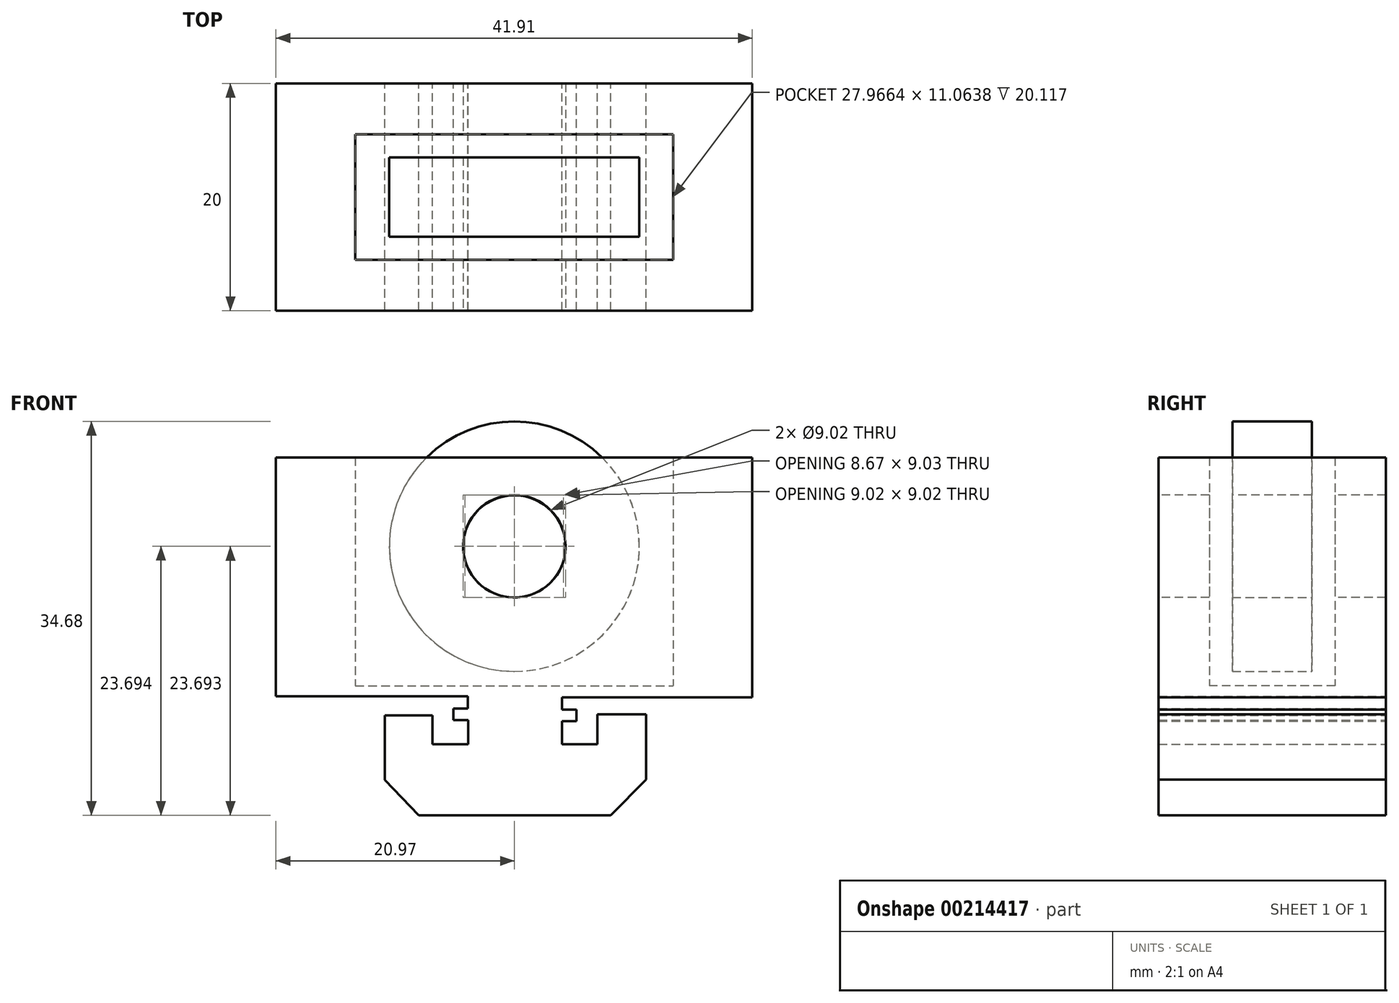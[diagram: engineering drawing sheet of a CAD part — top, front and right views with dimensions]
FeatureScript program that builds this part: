
annotation { "Feature Type Name" : "Feature", "Feature Type Description" : "" }
export const myFeature = defineFeature(function(context is Context, id is Id, definition is map)
    precondition{}
    {
        {
            var Q0;
            Q0=qCreatedBy(makeId("Front.planeOp"),FACE);
            var sketch = newSketch(context, id + "F0", { "sketchPlane" : qUnion([Q0])});
            skLineSegment(sketch, "E0", {"start": v(-8.41, 44.65) * mm, "end": v(-11.4, 47.76) * mm});
            skLineSegment(sketch, "E1", {"start": v(-11.4, 47.76) * mm, "end": v(-11.4, 53.45) * mm});
            skLineSegment(sketch, "E2", {"start": v(-11.4, 53.45) * mm, "end": v(-7.2, 53.45) * mm});
            skLineSegment(sketch, "E3", {"start": v(-7.2, 53.45) * mm, "end": v(-7.2, 50.92) * mm});
            skLineSegment(sketch, "E4", {"start": v(-7.2, 50.92) * mm, "end": v(-4.06, 50.92) * mm});
            skLineSegment(sketch, "E5", {"start": v(-4.06, 50.92) * mm, "end": v(-4.06, 53.04) * mm});
            skLineSegment(sketch, "E6", {"start": v(-4.06, 53.04) * mm, "end": v(-5.36, 53.04) * mm});
            skLineSegment(sketch, "E7", {"start": v(-5.36, 53.04) * mm, "end": v(-5.36, 54.06) * mm});
            skLineSegment(sketch, "E8", {"start": v(-5.36, 54.06) * mm, "end": v(-4.09, 54.06) * mm});
            skLineSegment(sketch, "E9", {"start": v(-4.09, 54.06) * mm, "end": v(-4.09, 55.13) * mm});
            skLineSegment(sketch, "E10", {"start": v(4.21, 55.04) * mm, "end": v(4.21, 53.96) * mm});
            skLineSegment(sketch, "E11", {"start": v(4.21, 53.96) * mm, "end": v(5.48, 53.96) * mm});
            skLineSegment(sketch, "E12", {"start": v(5.48, 53.96) * mm, "end": v(5.48, 52.95) * mm});
            skLineSegment(sketch, "E13", {"start": v(5.48, 52.95) * mm, "end": v(4.18, 52.95) * mm});
            skLineSegment(sketch, "E14", {"start": v(4.18, 52.95) * mm, "end": v(4.18, 50.93) * mm});
            skLineSegment(sketch, "E15", {"start": v(4.18, 50.93) * mm, "end": v(7.32, 50.93) * mm});
            skLineSegment(sketch, "E16", {"start": v(7.32, 50.93) * mm, "end": v(7.32, 53.56) * mm});
            skLineSegment(sketch, "E17", {"start": v(7.32, 53.56) * mm, "end": v(11.6, 53.56) * mm});
            skLineSegment(sketch, "E18", {"start": v(11.6, 53.56) * mm, "end": v(11.6, 47.8) * mm});
            skLineSegment(sketch, "E19", {"start": v(11.6, 47.8) * mm, "end": v(8.47, 44.65) * mm});
            skLineSegment(sketch, "E20", {"start": v(-8.41, 44.65) * mm, "end": v(8.47, 44.65) * mm});
            skLineSegment(sketch, "E21", {"start": v(4.21, 55.04) * mm, "end": v(20.94, 55.04) * mm});
            skLineSegment(sketch, "E22", {"start": v(-4.09, 55.13) * mm, "end": v(-20.97, 55.13) * mm});
            skLineSegment(sketch, "E23", {"start": v(-20.97, 55.13) * mm, "end": v(-20.97, 56.05) * mm});
            skLineSegment(sketch, "E24", {"start": v(-20.97, 56.05) * mm, "end": v(20.94, 56.05) * mm});
            skLineSegment(sketch, "E25", {"start": v(20.94, 56.05) * mm, "end": v(20.94, 55.04) * mm});
            skPoint(sketch, "E26", {"position": v(-0.02, 56.05) * mm});
            skPoint(sketch, "E27", {"position": v(-0.02, 44.65) * mm});
            skSolve(sketch);
        }
        {
            var Q0;
            Q0=qCreatedBy(makeId("Front.planeOp"),FACE);
            var sketch = newSketch(context, id + "F1", { "sketchPlane" : qUnion([Q0])});
            skCircle(sketch, "E28", {"center": v(0, 68.33) * mm, "radius": 11 * mm});
            skCircle(sketch, "E29", {"center": v(0, 68.33) * mm, "radius": 4.5 * mm});
            skSolve(sketch);
        }
        {
            var Q0;
            Q0=makeQuery(id+"F1.imprint","IMPRINT",FACE,{"disambiguationData":[TD([[makeQuery(id+"F1.imprint","IMPRINT",EDGE,{"derivedFrom":sQuery(id+"F1.wireOp",EDGE,"E28")}),1.0]])]});
            extrude(context, id + "F2", {"entities" : qUnion([Q0]), "depth" : 3.5 * mm});
        }
        {
            var Q0;
            Q0 = qSketchRegion(id + "F0", true);
            var Q1;
            Q1=makeQuery(id+"F0.imprint","IMPRINT",FACE,{"disambiguationData":[TD([[makeQuery(id+"F0.imprint","IMPRINT",EDGE,{"derivedFrom":sQuery(id+"F0.wireOp",EDGE,"E0")}),-1.0]])]});
            extrude(context, id + "F3", {"entities" : qUnion([Q0, Q1]), "depth" : 10 * mm});
        }
        {
            var Q0;
            Q0=makeQuery(id+"F0.imprint","IMPRINT",FACE,{"disambiguationData":[TD([[makeQuery(id+"F0.imprint","IMPRINT",EDGE,{"derivedFrom":sQuery(id+"F0.wireOp",EDGE,"E0")}),-1.0]])]});
            extrude(context, id + "F4", {"entities" : qUnion([Q0]), "operationType" : NewBodyOperationType.ADD, "oppositeDirection" : true, "depth" : 10 * mm});
        }
        {
            var Q0;
            Q0=makeQuery(id+"F1.imprint","IMPRINT",FACE,{"disambiguationData":[TD([[makeQuery(id+"F1.imprint","IMPRINT",EDGE,{"derivedFrom":sQuery(id+"F1.wireOp",EDGE,"E28")}),1.0]])]});
            extrude(context, id + "F5", {"entities" : qUnion([Q0]), "operationType" : NewBodyOperationType.ADD, "oppositeDirection" : true, "depth" : 3.5 * mm});
        }
        {
            var Q0;
            {var subQ0=sQuery(id+"F0.wireOp",EDGE,"E24");Q0=makeQuery(id+"F4.boolean.opBoolean","MERGE",FACE,{"derivedFrom":[makeQuery(id+"F3.opExtrude","SWEPT_FACE",FACE,{"disambiguationData":[OSD([subQ0])]}),makeQuery(id+"F4.opExtrude","SWEPT_FACE",FACE,{"disambiguationData":[OSD([subQ0])]})]});}
            var sketch = newSketch(context, id + "F6", { "sketchPlane" : qUnion([Q0])});
            skLineSegment(sketch, "E30.bottom", {"start": v(20.94, 10) * mm, "end": v(13.97, 10) * mm});
            skLineSegment(sketch, "E30.top", {"start": v(20.94, -10) * mm, "end": v(13.97, -10) * mm});
            skLineSegment(sketch, "E30.left", {"start": v(20.94, 10) * mm, "end": v(20.94, -10) * mm});
            skLineSegment(sketch, "E30.right", {"start": v(13.97, 10) * mm, "end": v(13.97, -10) * mm});
            skLineSegment(sketch, "E31.bottom", {"start": v(-20.97, 10) * mm, "end": v(-14, 10) * mm});
            skLineSegment(sketch, "E31.top", {"start": v(-20.97, -10) * mm, "end": v(-14, -10) * mm});
            skLineSegment(sketch, "E31.left", {"start": v(-20.97, 10) * mm, "end": v(-20.97, -10) * mm});
            skLineSegment(sketch, "E31.right", {"start": v(-14, 10) * mm, "end": v(-14, -10) * mm});
            skLineSegment(sketch, "E32.bottom", {"start": v(-14, 10) * mm, "end": v(13.97, 10) * mm});
            skLineSegment(sketch, "E32.top", {"start": v(-14, 5.53) * mm, "end": v(13.97, 5.53) * mm});
            skLineSegment(sketch, "E32.left", {"start": v(-14, 10) * mm, "end": v(-14, 5.53) * mm});
            skLineSegment(sketch, "E32.right", {"start": v(13.97, 10) * mm, "end": v(13.97, 5.53) * mm});
            skLineSegment(sketch, "E33.bottom", {"start": v(-14, -10) * mm, "end": v(13.97, -10) * mm});
            skLineSegment(sketch, "E33.top", {"start": v(-14, -5.53) * mm, "end": v(13.97, -5.53) * mm});
            skLineSegment(sketch, "E33.left", {"start": v(-14, -10) * mm, "end": v(-14, -5.53) * mm});
            skLineSegment(sketch, "E33.right", {"start": v(13.97, -10) * mm, "end": v(13.97, -5.53) * mm});
            skSolve(sketch);
        }
        {
            var Q0;
            Q0 = qSketchRegion(id + "F6", true);
            extrude(context, id + "F7", {"entities" : qUnion([Q0]), "operationType" : NewBodyOperationType.ADD, "depth" : 20.12 * mm});
        }
        {
            var Q0;
            Q0=makeQuery(id+"F7.boolean.opBoolean","MERGE",FACE,{"derivedFrom":[makeQuery(id+"F3.opExtrude","CAP_FACE",FACE,{"disambiguationData":[OSD([sQuery(id+"F0.wireOp",EDGE,"E0"),sQuery(id+"F0.wireOp",EDGE,"E1"),sQuery(id+"F0.wireOp",EDGE,"E2"),sQuery(id+"F0.wireOp",EDGE,"E3"),sQuery(id+"F0.wireOp",EDGE,"E4"),sQuery(id+"F0.wireOp",EDGE,"E5"),sQuery(id+"F0.wireOp",EDGE,"E6"),sQuery(id+"F0.wireOp",EDGE,"E7"),sQuery(id+"F0.wireOp",EDGE,"E8"),sQuery(id+"F0.wireOp",EDGE,"E9"),sQuery(id+"F0.wireOp",EDGE,"E10"),sQuery(id+"F0.wireOp",EDGE,"E11"),sQuery(id+"F0.wireOp",EDGE,"E12"),sQuery(id+"F0.wireOp",EDGE,"E13"),sQuery(id+"F0.wireOp",EDGE,"E14"),sQuery(id+"F0.wireOp",EDGE,"E15"),sQuery(id+"F0.wireOp",EDGE,"E16"),sQuery(id+"F0.wireOp",EDGE,"E17"),sQuery(id+"F0.wireOp",EDGE,"E18"),sQuery(id+"F0.wireOp",EDGE,"E19"),sQuery(id+"F0.wireOp",EDGE,"E20"),sQuery(id+"F0.wireOp",EDGE,"E21"),sQuery(id+"F0.wireOp",EDGE,"E22"),sQuery(id+"F0.wireOp",EDGE,"E23"),sQuery(id+"F0.wireOp",EDGE,"E24"),sQuery(id+"F0.wireOp",EDGE,"E25")])],"isStart":false}),makeQuery(id+"F7.opExtrude","SWEPT_FACE",FACE,{"disambiguationData":[OSD([sQuery(id+"F6.wireOp",EDGE,"E30.top"),sQuery(id+"F6.wireOp",EDGE,"E31.top"),sQuery(id+"F6.wireOp",EDGE,"E33.bottom")])]})]});
            var sketch = newSketch(context, id + "F8", { "sketchPlane" : qUnion([Q0])});
            skCircle(sketch, "E34", {"center": v(0, 68.34) * mm, "radius": 4.51 * mm});
            skSolve(sketch);
        }
        {
            var Q0;
            Q0=sQuery(id+"F8.wireOp",VERTEX,"E34.center");
            var Q1;
            Q1=makeQuery(id+"F3.opExtrude","SWEPT_BODY",BODY,{"disambiguationData":[OSD([sQuery(id+"F0.wireOp",EDGE,"E0"),sQuery(id+"F0.wireOp",EDGE,"E1"),sQuery(id+"F0.wireOp",EDGE,"E2"),sQuery(id+"F0.wireOp",EDGE,"E3"),sQuery(id+"F0.wireOp",EDGE,"E4"),sQuery(id+"F0.wireOp",EDGE,"E5"),sQuery(id+"F0.wireOp",EDGE,"E6"),sQuery(id+"F0.wireOp",EDGE,"E7"),sQuery(id+"F0.wireOp",EDGE,"E8"),sQuery(id+"F0.wireOp",EDGE,"E9"),sQuery(id+"F0.wireOp",EDGE,"E10"),sQuery(id+"F0.wireOp",EDGE,"E11"),sQuery(id+"F0.wireOp",EDGE,"E12"),sQuery(id+"F0.wireOp",EDGE,"E13"),sQuery(id+"F0.wireOp",EDGE,"E14"),sQuery(id+"F0.wireOp",EDGE,"E15"),sQuery(id+"F0.wireOp",EDGE,"E16"),sQuery(id+"F0.wireOp",EDGE,"E17"),sQuery(id+"F0.wireOp",EDGE,"E18"),sQuery(id+"F0.wireOp",EDGE,"E19"),sQuery(id+"F0.wireOp",EDGE,"E20"),sQuery(id+"F0.wireOp",EDGE,"E21"),sQuery(id+"F0.wireOp",EDGE,"E22"),sQuery(id+"F0.wireOp",EDGE,"E23"),sQuery(id+"F0.wireOp",EDGE,"E24"),sQuery(id+"F0.wireOp",EDGE,"E25")])]});
            var Q2;
            Q2=makeQuery(id+"F2.opExtrude","SWEPT_BODY",BODY,{"disambiguationData":[OSD([sQuery(id+"F1.wireOp",EDGE,"E28"),sQuery(id+"F1.wireOp",EDGE,"E29")])]});
            hole(context, id + "F9", {"style" : HoleStyle.SIMPLE, "endStyle" : HoleEndStyle.THROUGH, "holeDiameter" : 9.02 * mm, "locations" : qUnion([Q0]), "scope" : qUnion([Q1, Q2]), "isTappedThrough" : true});
        }
    });
